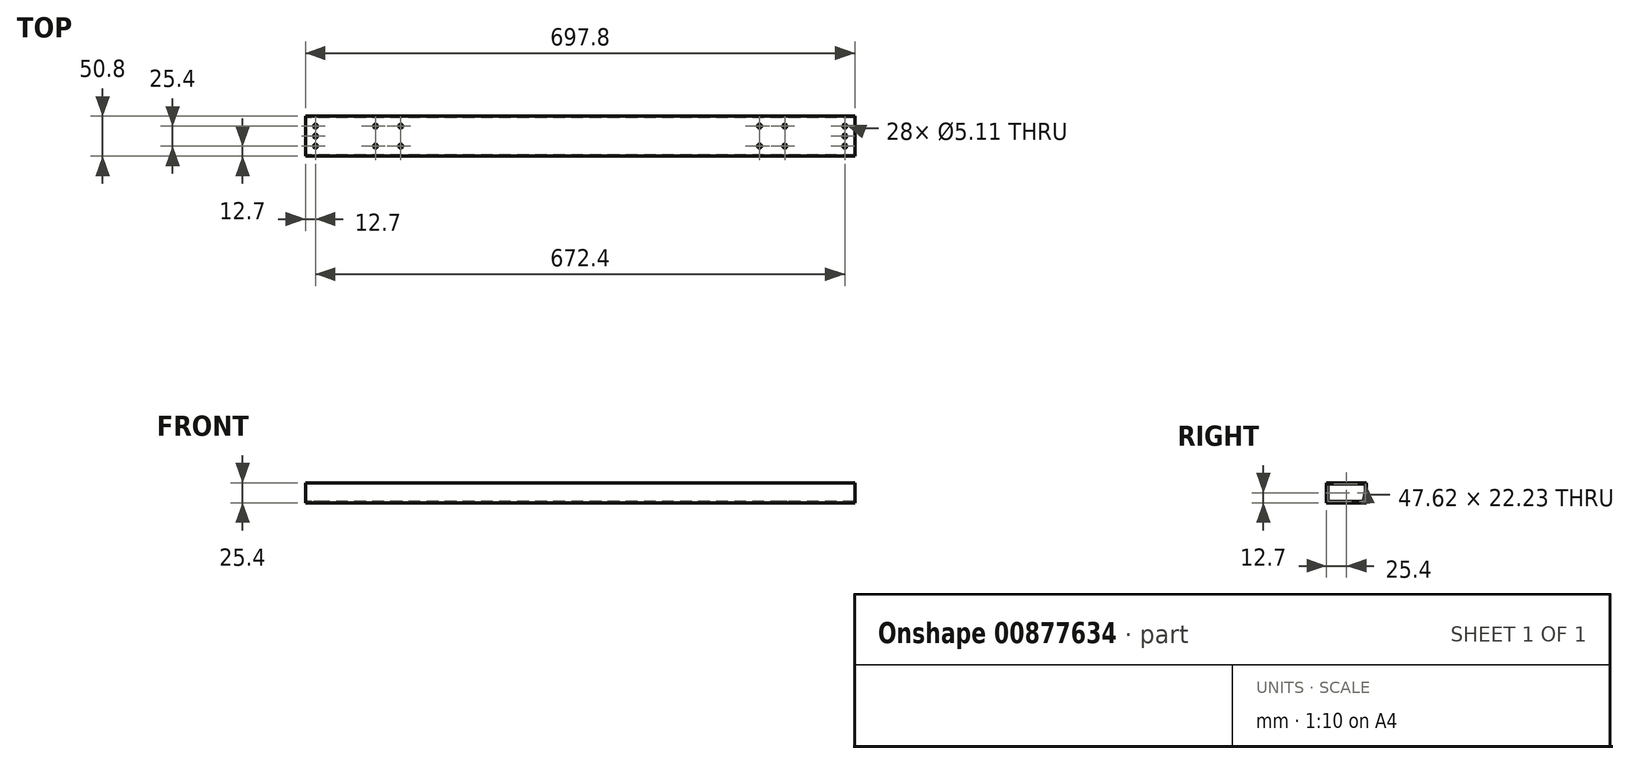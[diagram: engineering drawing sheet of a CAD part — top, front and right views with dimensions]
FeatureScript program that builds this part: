
annotation { "Feature Type Name" : "Feature", "Feature Type Description" : "" }
export const myFeature = defineFeature(function(context is Context, id is Id, definition is map)
    precondition{}
    {
        {
            var Q0;
            Q0=qCreatedBy(makeId("Top.planeOp"),FACE);
            var sketch = newSketch(context, id + "F0", { "sketchPlane" : qUnion([Q0])});
            skLineSegment(sketch, "E0.bottom", {"start": v(-348.9, 25.4) * mm, "end": v(348.9, 25.4) * mm});
            skLineSegment(sketch, "E0.top", {"start": v(-348.9, -25.4) * mm, "end": v(348.9, -25.4) * mm});
            skLineSegment(sketch, "E0.left", {"start": v(-348.9, 25.4) * mm, "end": v(-348.9, -25.4) * mm});
            skLineSegment(sketch, "E0.right", {"start": v(348.9, 25.4) * mm, "end": v(348.9, -25.4) * mm});
            skPoint(sketch, "E0.middle", {"position": v(0, 0) * mm});
            skCircle(sketch, "E1", {"center": v(-336.2, 12.7) * mm, "radius": 2.55 * mm});
            skCircle(sketch, "E2.0.1.0", {"center": v(-336.2, 0) * mm, "radius": 2.55 * mm});
            skCircle(sketch, "E2.0.2.0", {"center": v(-336.2, -12.7) * mm, "radius": 2.55 * mm});
            skLineSegment(sketch, "E2.direction1", {"start": v(-336.2, 12.7) * mm, "end": v(-285.4, 12.7) * mm, "construction": true});
            skLineSegment(sketch, "E2.direction2", {"start": v(-336.2, 12.7) * mm, "end": v(-336.2, 0) * mm, "construction": true});
            skCircle(sketch, "E3", {"center": v(336.2, 12.7) * mm, "radius": 2.55 * mm});
            skCircle(sketch, "E4.0.1.0", {"center": v(336.2, 0) * mm, "radius": 2.55 * mm});
            skCircle(sketch, "E4.0.2.0", {"center": v(336.2, -12.7) * mm, "radius": 2.55 * mm});
            skLineSegment(sketch, "E4.direction1", {"start": v(336.2, 12.7) * mm, "end": v(336.2, 12.7) * mm});
            skLineSegment(sketch, "E4.direction2", {"start": v(336.2, 12.7) * mm, "end": v(336.2, 0) * mm, "construction": true});
            skSolve(sketch);
        }
        {
            var Q0;
            Q0=makeQuery(id+"F0.imprint","IMPRINT",FACE,{"disambiguationData":[TD([[makeQuery(id+"F0.imprint","IMPRINT",EDGE,{"derivedFrom":sQuery(id+"F0.wireOp",EDGE,"E0.bottom")}),-1.0]])]});
            extrude(context, id + "F1", {"entities" : qUnion([Q0]), "depth" : 25.4 * mm, "offsetDistance" : 25.4 * mm});
        }
        {
            var Q0;
            Q0=makeQuery(id+"F1.opExtrude","SWEPT_FACE",FACE,{"disambiguationData":[OSD([sQuery(id+"F0.wireOp",EDGE,"E0.left")])]});
            var sketch = newSketch(context, id + "F2", { "sketchPlane" : qUnion([Q0])});
            skLineSegment(sketch, "E5.bottom", {"start": v(23.81, 23.81) * mm, "end": v(-23.81, 23.81) * mm});
            skLineSegment(sketch, "E5.top", {"start": v(23.81, 1.59) * mm, "end": v(-23.81, 1.59) * mm});
            skLineSegment(sketch, "E5.left", {"start": v(23.81, 23.81) * mm, "end": v(23.81, 1.59) * mm});
            skLineSegment(sketch, "E5.right", {"start": v(-23.81, 23.81) * mm, "end": v(-23.81, 1.59) * mm});
            skPoint(sketch, "E5.middle", {"position": v(0, 12.7) * mm});
            skPoint(sketch, "E5.middle.positionSnap0", {"position": v(-25.4, 12.7) * mm});
            skPoint(sketch, "E5.centerSnap0", {"position": v(-25.4, 12.7) * mm});
            skSolve(sketch);
        }
        {
            var Q0;
            Q0 = qSketchRegion(id + "F2", true);
            extrude(context, id + "F3", {"entities" : qUnion([Q0]), "operationType" : NewBodyOperationType.REMOVE, "endBound" : BoundingType.THROUGH_ALL, "oppositeDirection" : true, "depth" : 25.4 * mm, "offsetDistance" : 25.4 * mm});
        }
        {
            var Q0;
            Q0=makeQuery(id+"F1.opExtrude","CAP_FACE",FACE,{"disambiguationData":[OSD([sQuery(id+"F0.wireOp",EDGE,"E0.bottom"),sQuery(id+"F0.wireOp",EDGE,"E0.top"),sQuery(id+"F0.wireOp",EDGE,"E0.left"),sQuery(id+"F0.wireOp",EDGE,"E0.right"),sQuery(id+"F0.wireOp",EDGE,"E1"),sQuery(id+"F0.wireOp",EDGE,"E2.0.1.0"),sQuery(id+"F0.wireOp",EDGE,"E2.0.2.0"),sQuery(id+"F0.wireOp",EDGE,"E3"),sQuery(id+"F0.wireOp",EDGE,"E4.0.1.0"),sQuery(id+"F0.wireOp",EDGE,"E4.0.2.0")])],"isStart":false});
            var sketch = newSketch(context, id + "F4", { "sketchPlane" : qUnion([Q0])});
            skLineSegment(sketch, "E6.bottom", {"start": v(-260, 12.7) * mm, "end": v(-227.84, 12.7) * mm, "construction": true});
            skLineSegment(sketch, "E6.top", {"start": v(-260, -12.7) * mm, "end": v(-227.84, -12.7) * mm, "construction": true});
            skLineSegment(sketch, "E6.left", {"start": v(-260, 12.7) * mm, "end": v(-260, -12.7) * mm, "construction": true});
            skLineSegment(sketch, "E6.right", {"start": v(-227.84, 12.7) * mm, "end": v(-227.84, -12.7) * mm, "construction": true});
            skPoint(sketch, "E6.middle", {"position": v(-243.92, 0) * mm});
            skLineSegment(sketch, "E7", {"start": v(0, 25.4) * mm, "end": v(0, -25.4) * mm, "construction": true});
            skLineSegment(sketch, "E8.MirrorCS", {"start": v(260, -12.7) * mm, "end": v(227.84, -12.7) * mm, "construction": true});
            skLineSegment(sketch, "E9.MirrorCS", {"start": v(260, 12.7) * mm, "end": v(260, -12.7) * mm, "construction": true});
            skLineSegment(sketch, "E10.MirrorCS", {"start": v(260, 12.7) * mm, "end": v(227.84, 12.7) * mm, "construction": true});
            skPoint(sketch, "E11.MirrorP", {"position": v(243.92, 0) * mm});
            skLineSegment(sketch, "E12.MirrorCS", {"start": v(227.84, 12.7) * mm, "end": v(227.84, -12.7) * mm, "construction": true});
            skCircle(sketch, "E13", {"center": v(-227.84, 12.7) * mm, "radius": 2.55 * mm});
            skCircle(sketch, "E14", {"center": v(-227.84, -12.7) * mm, "radius": 2.55 * mm});
            skCircle(sketch, "E15", {"center": v(-260, -12.7) * mm, "radius": 2.55 * mm});
            skCircle(sketch, "E16", {"center": v(-260, 12.7) * mm, "radius": 2.55 * mm});
            skCircle(sketch, "E17.MirrorC", {"center": v(227.84, 12.7) * mm, "radius": 2.55 * mm});
            skCircle(sketch, "E18.MirrorC", {"center": v(260, -12.7) * mm, "radius": 2.55 * mm});
            skCircle(sketch, "E19.MirrorC", {"center": v(227.84, -12.7) * mm, "radius": 2.55 * mm});
            skCircle(sketch, "E20.MirrorC", {"center": v(260, 12.7) * mm, "radius": 2.55 * mm});
            skSolve(sketch);
        }
        {
            var Q0;
            Q0 = qSketchRegion(id + "F4", true);
            extrude(context, id + "F5", {"entities" : qUnion([Q0]), "operationType" : NewBodyOperationType.REMOVE, "oppositeDirection" : true, "depth" : 25.4 * mm, "offsetDistance" : 25.4 * mm});
        }
    });
